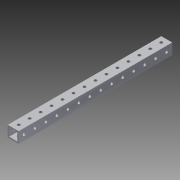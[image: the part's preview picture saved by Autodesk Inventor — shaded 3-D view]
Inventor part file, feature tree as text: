
AUTODESK INVENTOR PART (.ipt)
format: ipt  version: 2013 (Build 170138000, 138)  size: 167,424 bytes
history: native  units: in
note: dims shown in document units (in); Inventor stores cm internally (conversion verified against a paired STEP export)
features: extrude x3, sketch x3
ambient origin geometry x8: Origin, YZ Plane, XZ Plane, XY Plane, X Axis, Y Axis, Z Axis, Center Point
bodies: Solid1 (feature_tree)
feature tree (6):
  extrude  "Extrusion1"  Depth=1.0in
  extrude  "Extrusion2"  Depth=14.0in TaperAngle=0.0deg
  extrude  "Extrusion3"  Depth=0.26in
  sketch  "Sketch1"  dims[d0=1.0in d1=1.0in]
  sketch  "Sketch2"  dims[d2=0.125in d3=14.0in d4=0.0in]
  sketch  "Sketch3"  dims[d5=0.5in d7=0.26in d8=16.5in d9=0.0in d10=14.0in d11=5.5118in d13=1.0in d14=0.3937in d16=1.0in d19=0.5in d20=0.26in d21=0.26in d22=0.5in d23=0.26in d25=0.5in d26=5.5118in d28=1.0in d29=0.3937in d31=1.0in d34=1.0in d35=0.0in]
